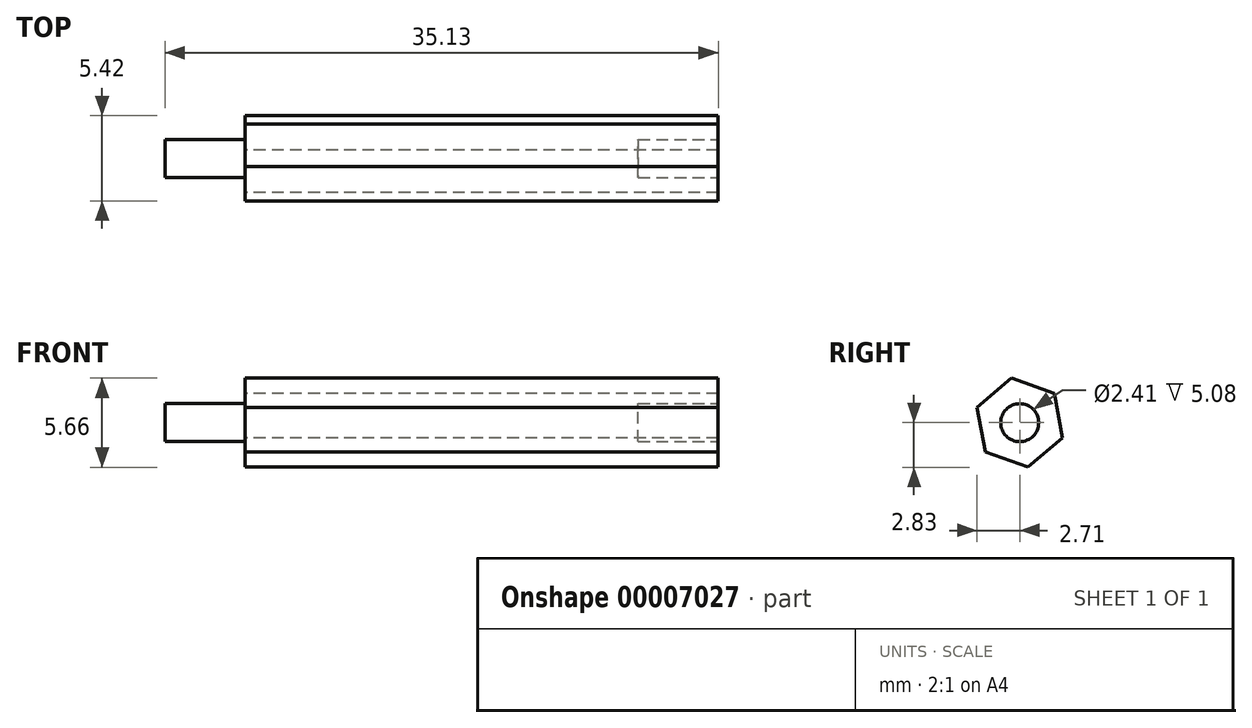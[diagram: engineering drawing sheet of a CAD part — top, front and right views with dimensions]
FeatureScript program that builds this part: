
annotation { "Feature Type Name" : "Feature", "Feature Type Description" : "" }
export const myFeature = defineFeature(function(context is Context, id is Id, definition is map)
    precondition{}
    {
        {
            var Q0;
            Q0=qCreatedBy(makeId("Right.planeOp"),FACE);
            var sketch = newSketch(context, id + "F0", { "sketchPlane" : qUnion([Q0])});
            skCircle(sketch, "E0.cCircle", {"center": v(0, 0) * mm, "radius": 2.49 * mm, "construction": true});
            skLineSegment(sketch, "E0.0", {"start": v(2.18, 1.87) * mm, "end": v(2.7, -0.96) * mm});
            skLineSegment(sketch, "E0.1", {"start": v(2.7, -0.96) * mm, "end": v(0.53, -2.83) * mm});
            skLineSegment(sketch, "E0.2", {"start": v(0.53, -2.83) * mm, "end": v(-2.18, -1.87) * mm});
            skLineSegment(sketch, "E0.3", {"start": v(-2.18, -1.87) * mm, "end": v(-2.7, 0.96) * mm});
            skLineSegment(sketch, "E0.4", {"start": v(-2.7, 0.96) * mm, "end": v(-0.53, 2.83) * mm});
            skLineSegment(sketch, "E0.5", {"start": v(-0.53, 2.83) * mm, "end": v(2.18, 1.87) * mm});
            skPoint(sketch, "E0.0.midPoint", {"position": v(2.45, 0.45) * mm});
            skSolve(sketch);
        }
        {
            var Q0;
            Q0 = qSketchRegion(id + "F0", true);
            extrude(context, id + "F1", {"entities" : qUnion([Q0]), "depth" : 30.05 * mm});
        }
        {
            var Q0;
            Q0=makeQuery(id+"F1.opExtrude","CAP_FACE",FACE,{"disambiguationData":[OSD([sQuery(id+"F0.wireOp",EDGE,"E0.0"),sQuery(id+"F0.wireOp",EDGE,"E0.1"),sQuery(id+"F0.wireOp",EDGE,"E0.2"),sQuery(id+"F0.wireOp",EDGE,"E0.3"),sQuery(id+"F0.wireOp",EDGE,"E0.4"),sQuery(id+"F0.wireOp",EDGE,"E0.5")])],"isStart":true});
            var sketch = newSketch(context, id + "F2", { "sketchPlane" : qUnion([Q0])});
            skCircle(sketch, "E1", {"center": v(0, 0) * mm, "radius": 1.2 * mm});
            skSolve(sketch);
        }
        {
            var Q0;
            Q0=makeQuery(id+"F1.opExtrude","CAP_FACE",FACE,{"disambiguationData":[OSD([sQuery(id+"F0.wireOp",EDGE,"E0.0"),sQuery(id+"F0.wireOp",EDGE,"E0.1"),sQuery(id+"F0.wireOp",EDGE,"E0.2"),sQuery(id+"F0.wireOp",EDGE,"E0.3"),sQuery(id+"F0.wireOp",EDGE,"E0.4"),sQuery(id+"F0.wireOp",EDGE,"E0.5")])],"isStart":false});
            var sketch = newSketch(context, id + "F3", { "sketchPlane" : qUnion([Q0])});
            skCircle(sketch, "E2", {"center": v(0, 0) * mm, "radius": 1.2 * mm});
            skSolve(sketch);
        }
        {
            var Q0;
            Q0 = qSketchRegion(id + "F3", true);
            var Q1;
            Q1 = qSketchRegion(id + "F0", true);
            extrude(context, id + "F4", {"entities" : qUnion([Q0, Q1]), "operationType" : NewBodyOperationType.REMOVE, "oppositeDirection" : true, "depth" : 5.08 * mm});
        }
        {
            var Q0;
            Q0 = qSketchRegion(id + "F2", true);
            extrude(context, id + "F5", {"entities" : qUnion([Q0]), "operationType" : NewBodyOperationType.ADD, "depth" : 5.08 * mm});
        }
    });
